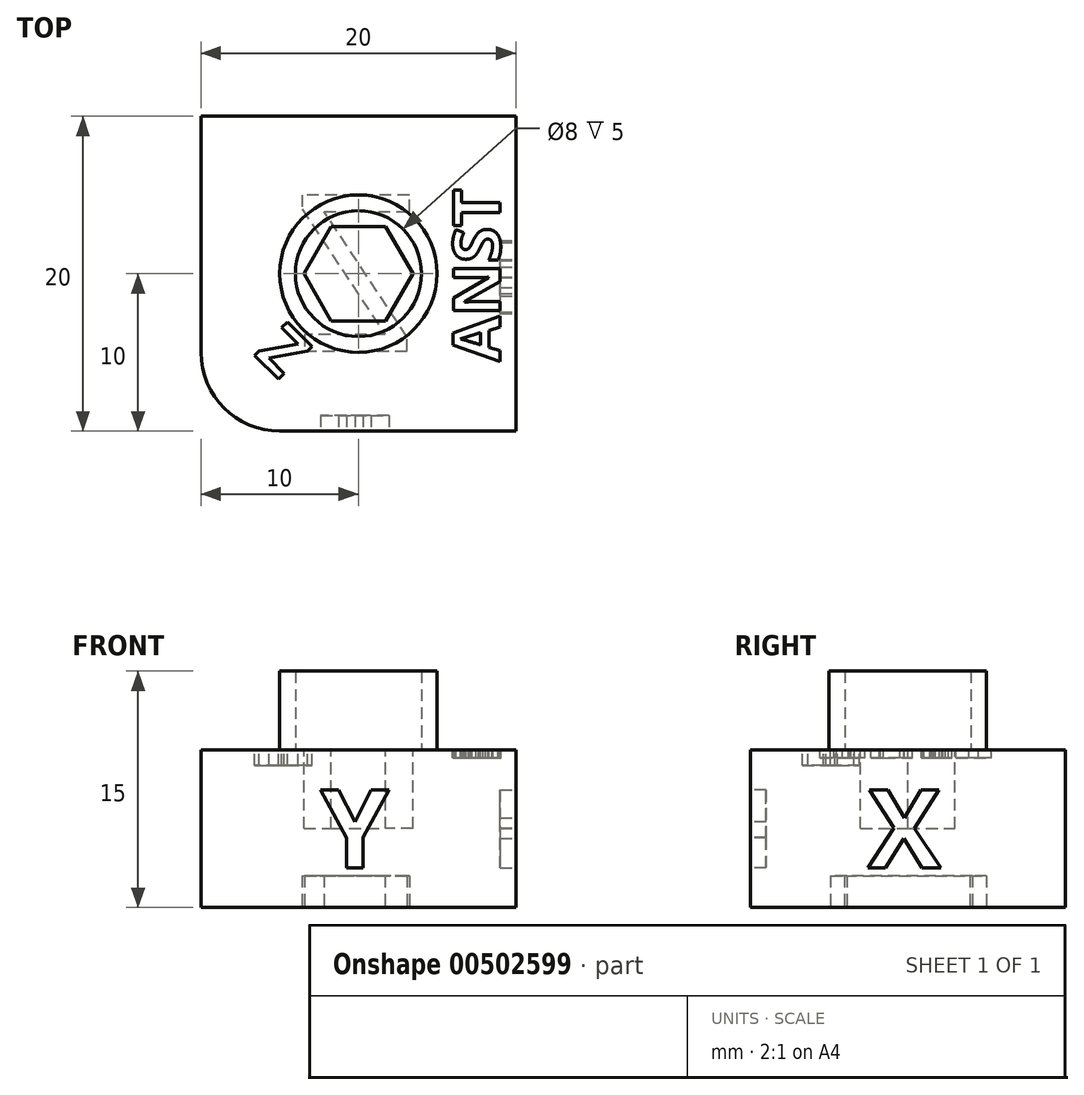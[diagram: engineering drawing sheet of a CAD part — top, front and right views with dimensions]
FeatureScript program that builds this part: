
annotation { "Feature Type Name" : "Feature", "Feature Type Description" : "" }
export const myFeature = defineFeature(function(context is Context, id is Id, definition is map)
    precondition{}
    {
        {
            var Q0;
            Q0=qCreatedBy(makeId("Top.planeOp"),FACE);
            var sketch = newSketch(context, id + "F0", { "sketchPlane" : qUnion([Q0])});
            skLineSegment(sketch, "E0.bottom", {"start": v(0, 0) * mm, "end": v(20, 0) * mm});
            skLineSegment(sketch, "E0.top", {"start": v(0, 20) * mm, "end": v(20, 20) * mm});
            skLineSegment(sketch, "E0.left", {"start": v(0, 0) * mm, "end": v(0, 20) * mm});
            skLineSegment(sketch, "E0.right", {"start": v(20, 0) * mm, "end": v(20, 20) * mm});
            skSolve(sketch);
        }
        {
            var Q0;
            Q0 = qSketchRegion(id + "F0", true);
            extrude(context, id + "F1", {"entities" : qUnion([Q0]), "depth" : 10 * mm});
        }
        {
            var Q0;
            Q0=makeQuery(id+"F1.opExtrude","CAP_FACE",FACE,{"disambiguationData":[OSD([sQuery(id+"F0.wireOp",EDGE,"E0.bottom"),sQuery(id+"F0.wireOp",EDGE,"E0.top"),sQuery(id+"F0.wireOp",EDGE,"E0.left"),sQuery(id+"F0.wireOp",EDGE,"E0.right")])],"isStart":false});
            var sketch = newSketch(context, id + "F2", { "sketchPlane" : qUnion([Q0])});
            skLineSegment(sketch, "E1", {"start": v(0, 0) * mm, "end": v(20, 20) * mm, "construction": true});
            skCircle(sketch, "E2", {"center": v(10, 10) * mm, "radius": 5 * mm});
            skCircle(sketch, "E3", {"center": v(10, 10) * mm, "radius": 4 * mm});
            skSolve(sketch);
        }
        {
            var Q0;
            Q0 = qSketchRegion(id + "F2", true);
            extrude(context, id + "F3", {"entities" : qUnion([Q0]), "operationType" : NewBodyOperationType.ADD, "depth" : 5 * mm});
        }
        {
            var Q0;
            Q0=makeQuery(id+"F1.opExtrude","CAP_FACE",FACE,{"disambiguationData":[OSD([sQuery(id+"F0.wireOp",EDGE,"E0.bottom"),sQuery(id+"F0.wireOp",EDGE,"E0.top"),sQuery(id+"F0.wireOp",EDGE,"E0.left"),sQuery(id+"F0.wireOp",EDGE,"E0.right")])],"isStart":true});
            var sketch = newSketch(context, id + "F4", { "sketchPlane" : qUnion([Q0])});
            skText(sketch, "E4", { "text": "Z", "fontName": "OpenSans-Regular.ttf"});
            skPoint(sketch, "E5", {"position": v(5.86, -10) * mm});
            const initialGuessF4  = {"E4": [0.00586, -0.015, 1, 0, 0.01]};
            skSetInitialGuess(sketch, initialGuessF4);
            skSolve(sketch);
        }
        {
            var Q0;
            Q0 = qSketchRegion(id + "F4", true);
            extrude(context, id + "F5", {"entities" : qUnion([Q0]), "operationType" : NewBodyOperationType.REMOVE, "oppositeDirection" : true, "depth" : 2 * mm});
        }
        {
            var Q0;
            Q0=makeQuery(id+"F1.opExtrude","SWEPT_FACE",FACE,{"disambiguationData":[OSD([sQuery(id+"F0.wireOp",EDGE,"E0.bottom")])]});
            var sketch = newSketch(context, id + "F6", { "sketchPlane" : qUnion([Q0])});
            skText(sketch, "E6", { "text": "Y", "fontName": "OpenSans-Bold.ttf"});
            skPoint(sketch, "E7", {"position": v(7.6, 5) * mm});
            const initialGuessF6  = {"E6": [0.0076, 0.0025, 1, 0, 0.005]};
            skSetInitialGuess(sketch, initialGuessF6);
            skSolve(sketch);
        }
        {
            var Q0;
            Q0 = qSketchRegion(id + "F6", true);
            extrude(context, id + "F7", {"entities" : qUnion([Q0]), "operationType" : NewBodyOperationType.REMOVE, "oppositeDirection" : true, "depth" : 1 * mm});
        }
        {
            var Q0;
            Q0=makeQuery(id+"F1.opExtrude","SWEPT_FACE",FACE,{"disambiguationData":[OSD([sQuery(id+"F0.wireOp",EDGE,"E0.right")])]});
            var sketch = newSketch(context, id + "F8", { "sketchPlane" : qUnion([Q0])});
            skText(sketch, "E8", { "text": "X", "fontName": "OpenSans-Bold.ttf"});
            skPoint(sketch, "E9.positionSnap0", {"position": v(0, 5) * mm});
            skPoint(sketch, "E10", {"position": v(7.46, 5) * mm});
            const initialGuessF8  = {"E8": [0.00746, 0.0025, 1, 0, 0.005]};
            skSetInitialGuess(sketch, initialGuessF8);
            skSolve(sketch);
        }
        {
            var Q0;
            Q0 = qSketchRegion(id + "F8", true);
            extrude(context, id + "F9", {"entities" : qUnion([Q0]), "operationType" : NewBodyOperationType.REMOVE, "oppositeDirection" : true, "depth" : 1 * mm});
        }
        {
            var Q0;
            Q0=makeQuery(id+"F1.opExtrude","SWEPT_EDGE",EDGE,{"disambiguationData":[OSD([sQuery(id+"F0.wireOp",EDGE,"E0.bottom"),sQuery(id+"F0.wireOp",EDGE,"E0.left")])]});
            fillet(context, id + "F10", {"entities" : qUnion([Q0]), "radius" : 5 * mm, "tangentPropagation" : true, "allowEdgeOverflow" : false});
        }
        {
            var Q0;
            {var subQ0=sQuery(id+"F0.wireOp",EDGE,"E0.left");var subQ1=sQuery(id+"F0.wireOp",EDGE,"E0.top");var subQ2=sQuery(id+"F0.wireOp",EDGE,"E0.right");var subQ3=sQuery(id+"F0.wireOp",EDGE,"E0.bottom");Q0=makeQuery(id+"F3.boolean.opBoolean","SPLIT",FACE,{"disambiguationData":[TD([makeQuery(id+"F1.opExtrude","SWEPT_FACE",FACE,{"disambiguationData":[OSD([subQ3])]})])],"derivedFrom":makeQuery(id+"F1.opExtrude","CAP_FACE",FACE,{"disambiguationData":[OSD([subQ3,subQ1,subQ0,subQ2])],"isStart":false})});}
            var sketch = newSketch(context, id + "F11", { "sketchPlane" : qUnion([Q0])});
            skText(sketch, "E11", { "text": "Z", "fontName": "OpenSans-Bold.ttf"});
            skLineSegment(sketch, "E12", {"start": v(3.17, 5) * mm, "end": v(0, 5) * mm, "construction": true});
            skLineSegment(sketch, "E13", {"start": v(5, 3.17) * mm, "end": v(5, 0) * mm, "construction": true});
            const initialGuessF11  = {"E11": [0.00712, 0.0053, -0.7071, 0.7071, 0.003]};
            skSetInitialGuess(sketch, initialGuessF11);
            skSolve(sketch);
        }
        {
            var Q0;
            Q0 = qSketchRegion(id + "F11", true);
            extrude(context, id + "F12", {"entities" : qUnion([Q0]), "operationType" : NewBodyOperationType.REMOVE, "oppositeDirection" : true, "depth" : 1 * mm});
        }
        {
            var Q0;
            {var subQ0=sQuery(id+"F0.wireOp",EDGE,"E0.left");var subQ1=sQuery(id+"F0.wireOp",EDGE,"E0.top");var subQ2=sQuery(id+"F0.wireOp",EDGE,"E0.right");var subQ3=sQuery(id+"F0.wireOp",EDGE,"E0.bottom");Q0=makeQuery(id+"F3.boolean.opBoolean","SPLIT",FACE,{"disambiguationData":[TD([makeQuery(id+"F1.opExtrude","SWEPT_FACE",FACE,{"disambiguationData":[OSD([subQ3])]})])],"derivedFrom":makeQuery(id+"F1.opExtrude","CAP_FACE",FACE,{"disambiguationData":[OSD([subQ3,subQ1,subQ0,subQ2])],"isStart":false})});}
            var sketch = newSketch(context, id + "F13", { "sketchPlane" : qUnion([Q0])});
            skText(sketch, "E14", { "text": "ANST", "fontName": "OpenSans-Bold.ttf"});
            const initialGuessF13  = {"E14": [0.019, 0.00442, 0, 1, 0.003]};
            skSetInitialGuess(sketch, initialGuessF13);
            skSolve(sketch);
        }
        {
            var Q0;
            Q0 = qSketchRegion(id + "F13", true);
            extrude(context, id + "F14", {"entities" : qUnion([Q0]), "operationType" : NewBodyOperationType.REMOVE, "oppositeDirection" : true, "depth" : 0.5 * mm});
        }
        {
            var Q0;
            Q0=makeQuery(id+"F3.boolean.opBoolean","SPLIT",FACE,{"disambiguationData":[TD([makeQuery(id+"F3.opExtrude","SWEPT_FACE",FACE,{"disambiguationData":[OSD([sQuery(id+"F2.wireOp",EDGE,"E3")])]})])],"derivedFrom":makeQuery(id+"F1.opExtrude","CAP_FACE",FACE,{"disambiguationData":[OSD([sQuery(id+"F0.wireOp",EDGE,"E0.bottom"),sQuery(id+"F0.wireOp",EDGE,"E0.top"),sQuery(id+"F0.wireOp",EDGE,"E0.left"),sQuery(id+"F0.wireOp",EDGE,"E0.right")])],"isStart":false})});
            var sketch = newSketch(context, id + "F15", { "sketchPlane" : qUnion([Q0])});
            skCircle(sketch, "E15.cCircle", {"center": v(10, 10) * mm, "radius": 3 * mm, "construction": true});
            skLineSegment(sketch, "E15.0", {"start": v(8.27, 13) * mm, "end": v(11.73, 13) * mm});
            skLineSegment(sketch, "E15.1", {"start": v(11.73, 13) * mm, "end": v(13.46, 10) * mm});
            skLineSegment(sketch, "E15.2", {"start": v(13.46, 10) * mm, "end": v(11.73, 7) * mm});
            skLineSegment(sketch, "E15.3", {"start": v(11.73, 7) * mm, "end": v(8.27, 7) * mm});
            skLineSegment(sketch, "E15.4", {"start": v(8.27, 7) * mm, "end": v(6.54, 10) * mm});
            skLineSegment(sketch, "E15.5", {"start": v(6.54, 10) * mm, "end": v(8.27, 13) * mm});
            skPoint(sketch, "E15.0.midPoint", {"position": v(10, 13) * mm});
            skSolve(sketch);
        }
        {
            var Q0;
            Q0 = qSketchRegion(id + "F15", true);
            extrude(context, id + "F16", {"entities" : qUnion([Q0]), "operationType" : NewBodyOperationType.REMOVE, "oppositeDirection" : true, "depth" : 5 * mm});
        }
    });
